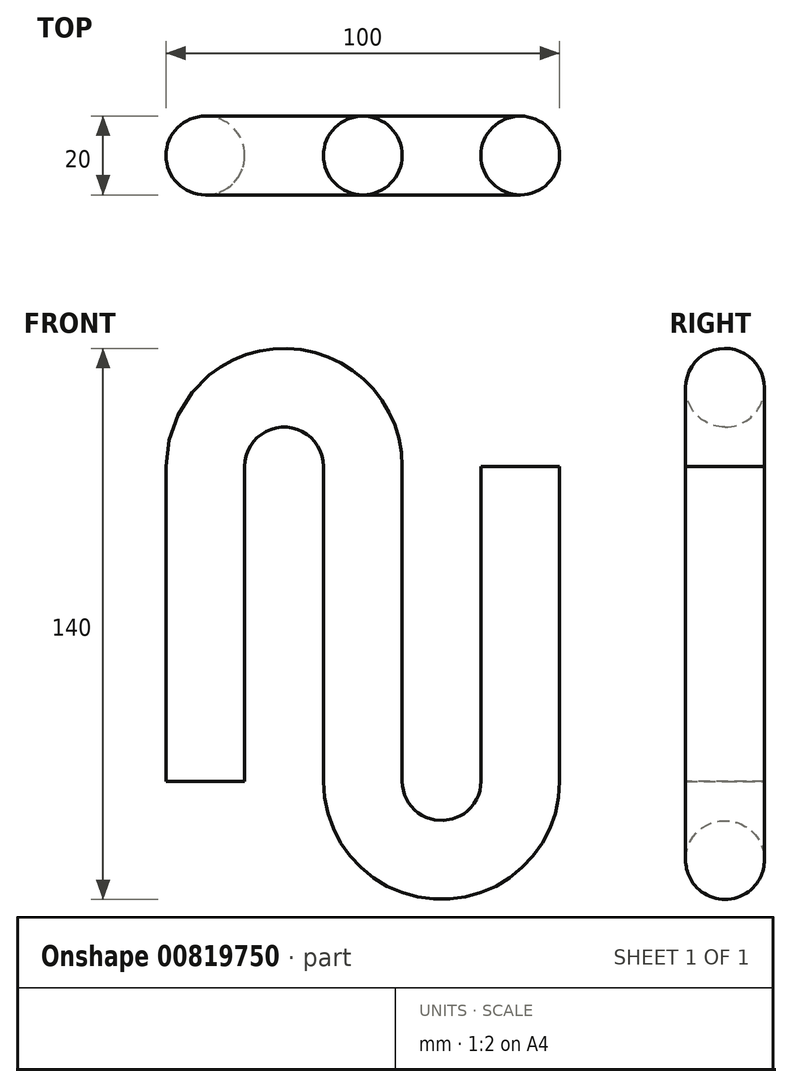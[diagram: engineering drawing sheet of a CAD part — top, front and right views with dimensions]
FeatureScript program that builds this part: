
annotation { "Feature Type Name" : "Feature", "Feature Type Description" : "" }
export const myFeature = defineFeature(function(context is Context, id is Id, definition is map)
    precondition{}
    {
        {
            var Q0;
            Q0=qCreatedBy(makeId("Front.planeOp"),FACE);
            var sketch = newSketch(context, id + "F0", { "sketchPlane" : qUnion([Q0])});
            skLineSegment(sketch, "E0", {"start": v(0, 0) * mm, "end": v(0, 80) * mm});
            skLineSegment(sketch, "E1", {"start": v(40, 80) * mm, "end": v(40, 0) * mm});
            skLineSegment(sketch, "E2", {"start": v(80, 0) * mm, "end": v(80, 80) * mm});
            skArc(sketch, "E3", {"start": v(40, 80) * mm, "mid": v(20, 100) * mm, "end": v(0, 80) * mm});
            skArc(sketch, "E4", {"start": v(40, 0) * mm, "mid": v(60, -20) * mm, "end": v(80, 0) * mm});
            skSolve(sketch);
        }
        {
            var Q0;
            Q0=qCreatedBy(makeId("Top.planeOp"),FACE);
            var sketch = newSketch(context, id + "F1", { "sketchPlane" : qUnion([Q0])});
            skCircle(sketch, "E5", {"center": v(0, 0) * mm, "radius": 10 * mm});
            skSolve(sketch);
        }
        {
            var Q0;
            Q0=makeQuery(id+"F1.imprint","IMPRINT",FACE,{"disambiguationData":[TD([[makeQuery(id+"F1.imprint","IMPRINT",EDGE,{"derivedFrom":sQuery(id+"F1.wireOp",EDGE,"E5")}),1.0]])]});
            var Q1;
            Q1 = qConstructionFilter(qBodyType(qCreatedBy(id + "F0" ,EDGE), BodyType.WIRE), ConstructionObject.NO);
            sweep(context, id + "F2", {"profiles" : qUnion([Q0]), "path" : qUnion([Q1])});
        }
    });
